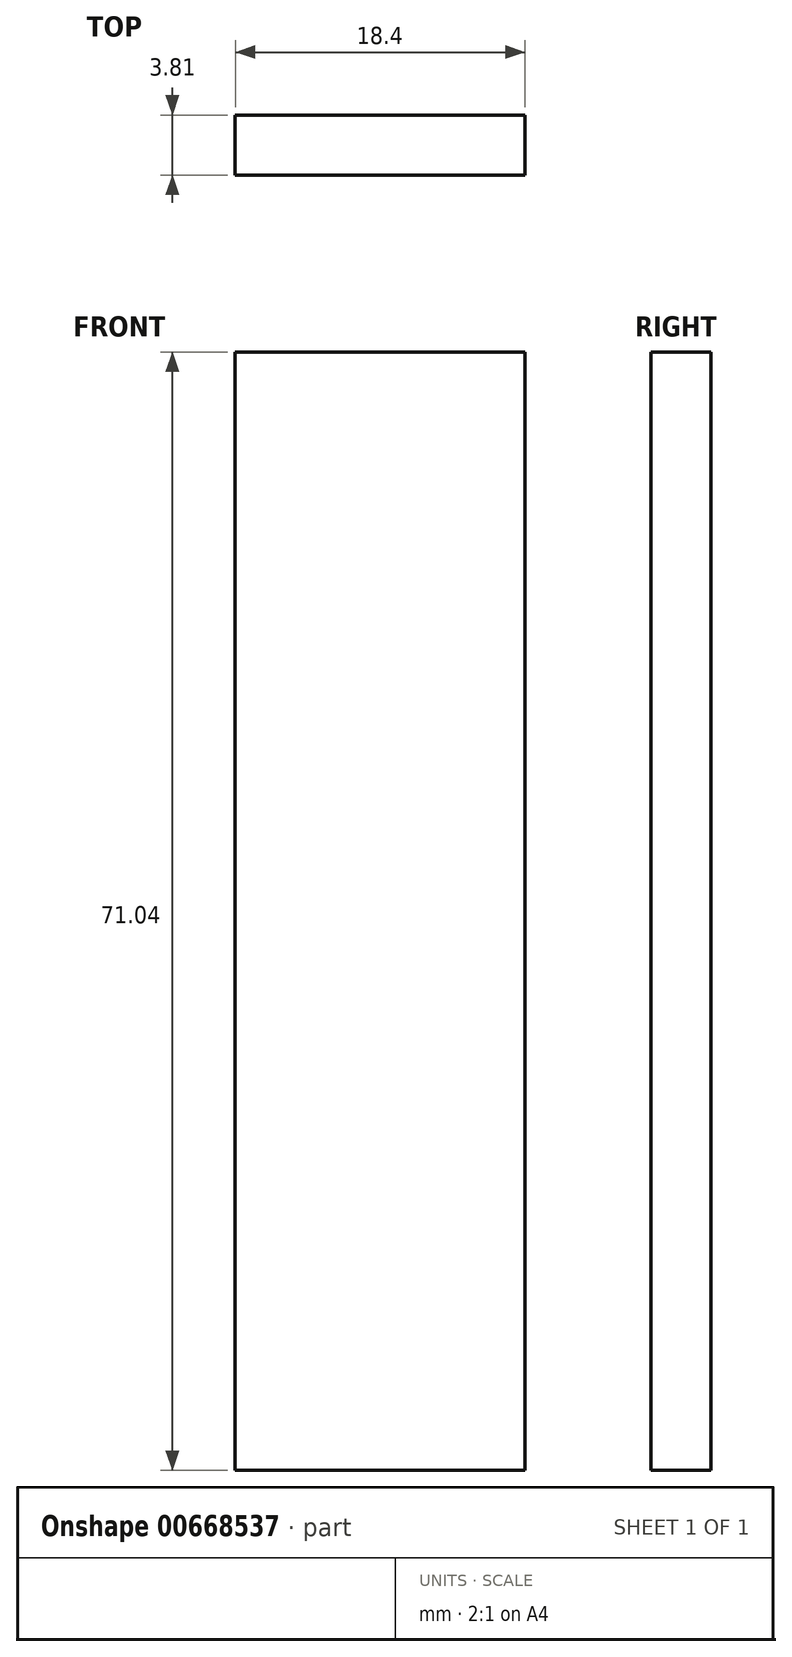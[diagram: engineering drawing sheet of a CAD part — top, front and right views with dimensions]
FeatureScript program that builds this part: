
annotation { "Feature Type Name" : "Feature", "Feature Type Description" : "" }
export const myFeature = defineFeature(function(context is Context, id is Id, definition is map)
    precondition{}
    {
        {
            var Q0;
            Q0=qCreatedBy(makeId("Front.planeOp"),FACE);
            var sketch = newSketch(context, id + "F0", { "sketchPlane" : qUnion([Q0])});
            skLineSegment(sketch, "E0.bottom", {"start": v(-9.2, -35.52) * mm, "end": v(9.2, -35.52) * mm});
            skLineSegment(sketch, "E0.top", {"start": v(-9.2, 35.52) * mm, "end": v(9.2, 35.52) * mm});
            skLineSegment(sketch, "E0.left", {"start": v(-9.2, -35.52) * mm, "end": v(-9.2, 35.52) * mm});
            skLineSegment(sketch, "E0.right", {"start": v(9.2, -35.52) * mm, "end": v(9.2, 35.52) * mm});
            skPoint(sketch, "E0.middle", {"position": v(0, 0) * mm});
            skSolve(sketch);
        }
        {
            var Q0;
            Q0=makeQuery(id+"F0.imprint","IMPRINT",FACE,{"disambiguationData":[TD([[makeQuery(id+"F0.imprint","IMPRINT",EDGE,{"derivedFrom":sQuery(id+"F0.wireOp",EDGE,"E0.bottom")}),1.0]])]});
            extrude(context, id + "F1", {"entities" : qUnion([Q0]), "depth" : 3.8 * mm, "offsetDistance" : 25.4 * mm});
        }
    });
